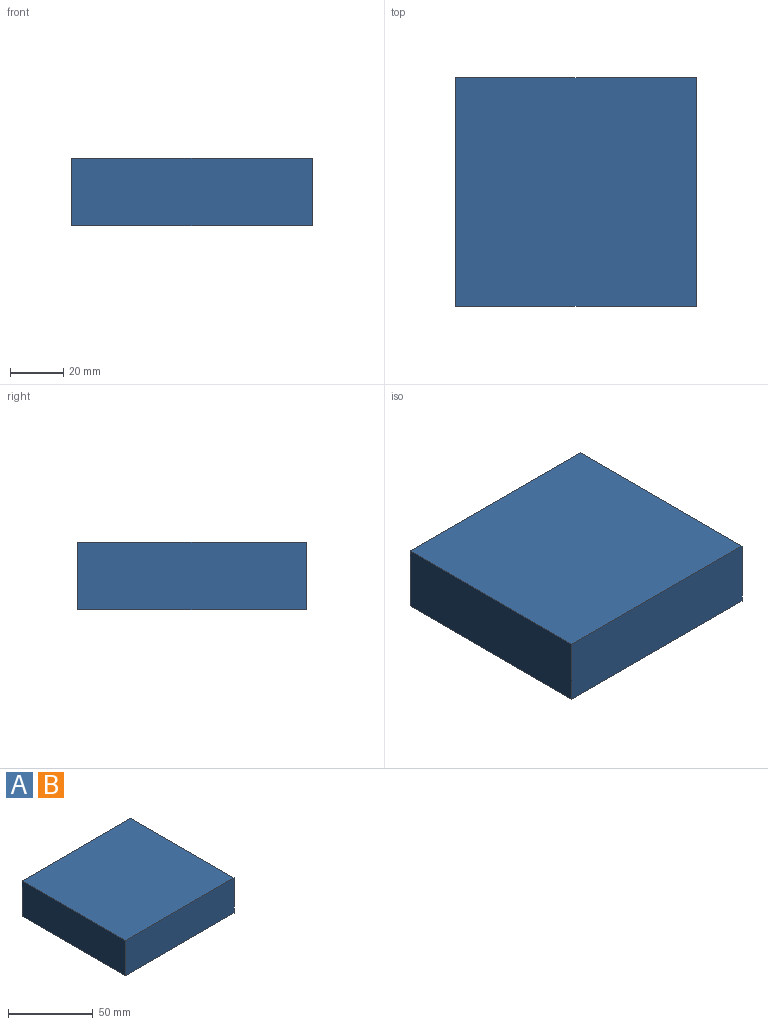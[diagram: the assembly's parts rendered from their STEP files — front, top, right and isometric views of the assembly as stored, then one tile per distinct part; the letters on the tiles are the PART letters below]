
ASSEMBLY  parts=2 mates=1
PART A: 6 faces, bbox 90.8x86.3x25.4 mm
  f0: plane 90.76x25.4mm, normal (0,1,0), area 2305.2mm2, adj f1,f3,f4,f5
  f1: plane 86.3x25.4mm, normal (-1,0,0), area 2192mm2, adj f0,f2,f4,f5
  f2: plane 90.76x25.4mm, normal (0,-1,0), area 2305.2mm2, adj f1,f3,f4,f5
  f3: plane 86.3x25.4mm, normal (1,0,0), area 2192mm2, adj f0,f2,f4,f5
  f4: plane 90.76x86.3mm, normal (0,0,1), area 7832.4mm2, adj f0,f1,f2,f3
  f5: plane 90.76x86.3mm, normal (0,0,-1), area 7832.4mm2, adj f0,f1,f2,f3
PART B: same geometry as A
PLACE A t=(51.56,-19.31,-48.49)mm
PLACE B t=(51.56,-19.31,-48.49)mm
MATE fastened B.f4 <-> A.f4  axis (0,0,1) through (6.18,-20.29,-23.09)mm
